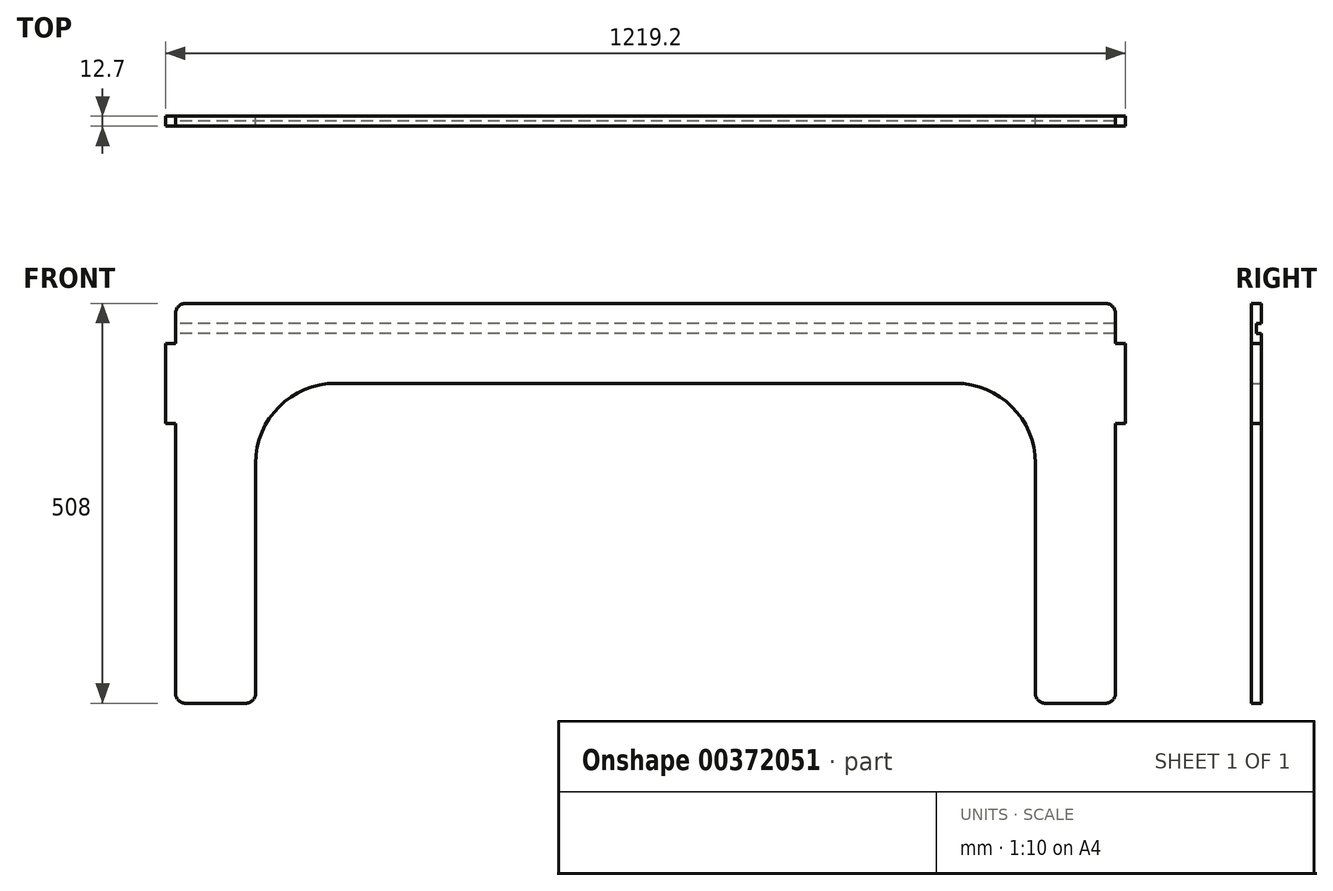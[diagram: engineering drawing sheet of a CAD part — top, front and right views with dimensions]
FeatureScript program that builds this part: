
annotation { "Feature Type Name" : "Feature", "Feature Type Description" : "" }
export const myFeature = defineFeature(function(context is Context, id is Id, definition is map)
    precondition{}
    {
        {
            var Q0;
            Q0=qCreatedBy(makeId("Front.planeOp"),FACE);
            var sketch = newSketch(context, id + "F0", { "sketchPlane" : qUnion([Q0])});
            skLineSegment(sketch, "E0.bottom", {"start": v(-467.73, -251.63) * mm, "end": v(-391.53, -251.63) * mm});
            skLineSegment(sketch, "E0.top", {"start": v(-467.73, 256.37) * mm, "end": v(700.67, 256.37) * mm});
            skLineSegment(sketch, "E0.left", {"start": v(-480.43, -238.93) * mm, "end": v(-480.43, 243.67) * mm});
            skLineSegment(sketch, "E0.right", {"start": v(713.37, -238.93) * mm, "end": v(713.37, 243.67) * mm});
            skLineSegment(sketch, "E1.top", {"start": v(-277.23, 154.77) * mm, "end": v(510.17, 154.77) * mm});
            skLineSegment(sketch, "E1.left", {"start": v(-378.83, -238.93) * mm, "end": v(-378.83, 53.17) * mm});
            skLineSegment(sketch, "E1.right", {"start": v(611.77, -238.93) * mm, "end": v(611.77, 53.17) * mm});
            skLineSegment(sketch, "E2.trimOffspring", {"start": v(624.47, -251.63) * mm, "end": v(700.67, -251.63) * mm});
            skPoint(sketch, "E3.visualSharp", {"position": v(-378.83, 154.77) * mm});
            skArc(sketch, "E3.filletArc", {"start": v(-277.23, 154.77) * mm, "mid": v(-349.07, 125.02) * mm, "end": v(-378.83, 53.17) * mm});
            skPoint(sketch, "E4.visualSharp", {"position": v(611.77, 154.77) * mm});
            skArc(sketch, "E4.filletArc", {"start": v(611.77, 53.17) * mm, "mid": v(582, 125.02) * mm, "end": v(510.17, 154.77) * mm});
            skPoint(sketch, "E5.visualSharp", {"position": v(-480.43, 256.37) * mm});
            skArc(sketch, "E5.filletArc", {"start": v(-467.73, 256.37) * mm, "mid": v(-476.71, 252.65) * mm, "end": v(-480.43, 243.67) * mm});
            skPoint(sketch, "E6.visualSharp", {"position": v(-480.43, -251.63) * mm});
            skArc(sketch, "E6.filletArc", {"start": v(-480.43, -238.93) * mm, "mid": v(-476.71, -247.9) * mm, "end": v(-467.73, -251.63) * mm});
            skPoint(sketch, "E7.visualSharp", {"position": v(-378.83, -251.63) * mm});
            skArc(sketch, "E7.filletArc", {"start": v(-391.53, -251.63) * mm, "mid": v(-382.55, -247.9) * mm, "end": v(-378.83, -238.93) * mm});
            skPoint(sketch, "E8.visualSharp", {"position": v(713.37, 256.37) * mm});
            skArc(sketch, "E8.filletArc", {"start": v(713.37, 243.67) * mm, "mid": v(709.65, 252.65) * mm, "end": v(700.67, 256.37) * mm});
            skPoint(sketch, "E9.visualSharp", {"position": v(713.37, -251.63) * mm});
            skArc(sketch, "E9.filletArc", {"start": v(700.67, -251.63) * mm, "mid": v(709.65, -247.9) * mm, "end": v(713.37, -238.93) * mm});
            skPoint(sketch, "E10.visualSharp", {"position": v(611.77, -251.63) * mm});
            skArc(sketch, "E10.filletArc", {"start": v(611.77, -238.93) * mm, "mid": v(615.49, -247.9) * mm, "end": v(624.47, -251.63) * mm});
            skLineSegment(sketch, "E11.bottom", {"start": v(713.37, 205.57) * mm, "end": v(726.07, 205.57) * mm});
            skLineSegment(sketch, "E11.top", {"start": v(713.37, 103.97) * mm, "end": v(726.07, 103.97) * mm});
            skLineSegment(sketch, "E11.left", {"start": v(713.37, 205.57) * mm, "end": v(713.37, 103.97) * mm});
            skLineSegment(sketch, "E11.right", {"start": v(726.07, 205.57) * mm, "end": v(726.07, 103.97) * mm});
            skLineSegment(sketch, "E12.bottom", {"start": v(-480.43, 205.57) * mm, "end": v(-493.13, 205.57) * mm});
            skLineSegment(sketch, "E12.top", {"start": v(-480.43, 103.97) * mm, "end": v(-493.13, 103.97) * mm});
            skLineSegment(sketch, "E12.left", {"start": v(-480.43, 205.57) * mm, "end": v(-480.43, 103.97) * mm});
            skLineSegment(sketch, "E12.right", {"start": v(-493.13, 205.57) * mm, "end": v(-493.13, 103.97) * mm});
            skSolve(sketch);
        }
        {
            var Q0;
            Q0 = qSketchRegion(id + "F0", true);
            extrude(context, id + "F1", {"entities" : qUnion([Q0]), "depth" : 12.7 * mm});
        }
        {
            var Q0;
            Q0=makeQuery(id+"F1.opExtrude","CAP_FACE",FACE,{"disambiguationData":[OSD([sQuery(id+"F0.wireOp",EDGE,"E0.bottom"),sQuery(id+"F0.wireOp",EDGE,"E0.top"),sQuery(id+"F0.wireOp",EDGE,"E0.left"),sQuery(id+"F0.wireOp",EDGE,"E0.right"),sQuery(id+"F0.wireOp",EDGE,"E1.top"),sQuery(id+"F0.wireOp",EDGE,"E1.left"),sQuery(id+"F0.wireOp",EDGE,"E1.right"),sQuery(id+"F0.wireOp",EDGE,"E2.trimOffspring"),sQuery(id+"F0.wireOp",EDGE,"E3.filletArc"),sQuery(id+"F0.wireOp",EDGE,"E4.filletArc"),sQuery(id+"F0.wireOp",EDGE,"E5.filletArc"),sQuery(id+"F0.wireOp",EDGE,"E6.filletArc"),sQuery(id+"F0.wireOp",EDGE,"E7.filletArc"),sQuery(id+"F0.wireOp",EDGE,"E8.filletArc"),sQuery(id+"F0.wireOp",EDGE,"E9.filletArc"),sQuery(id+"F0.wireOp",EDGE,"E10.filletArc"),sQuery(id+"F0.wireOp",EDGE,"E11.bottom"),sQuery(id+"F0.wireOp",EDGE,"E11.top"),sQuery(id+"F0.wireOp",EDGE,"E11.right"),sQuery(id+"F0.wireOp",EDGE,"E12.bottom"),sQuery(id+"F0.wireOp",EDGE,"E12.top"),sQuery(id+"F0.wireOp",EDGE,"E12.right")])],"isStart":true});
            var sketch = newSketch(context, id + "F2", { "sketchPlane" : qUnion([Q0])});
            skLineSegment(sketch, "E13.bottom", {"start": v(-713.37, 218.27) * mm, "end": v(480.43, 218.27) * mm});
            skLineSegment(sketch, "E13.top", {"start": v(-713.37, 230.97) * mm, "end": v(480.43, 230.97) * mm});
            skLineSegment(sketch, "E13.left", {"start": v(-713.37, 218.27) * mm, "end": v(-713.37, 230.97) * mm});
            skLineSegment(sketch, "E13.right", {"start": v(480.43, 218.27) * mm, "end": v(480.43, 230.97) * mm});
            skSolve(sketch);
        }
        {
            var Q0;
            Q0 = qSketchRegion(id + "F2", true);
            extrude(context, id + "F3", {"entities" : qUnion([Q0]), "operationType" : NewBodyOperationType.REMOVE, "oppositeDirection" : true, "depth" : 6.35 * mm});
        }
    });
